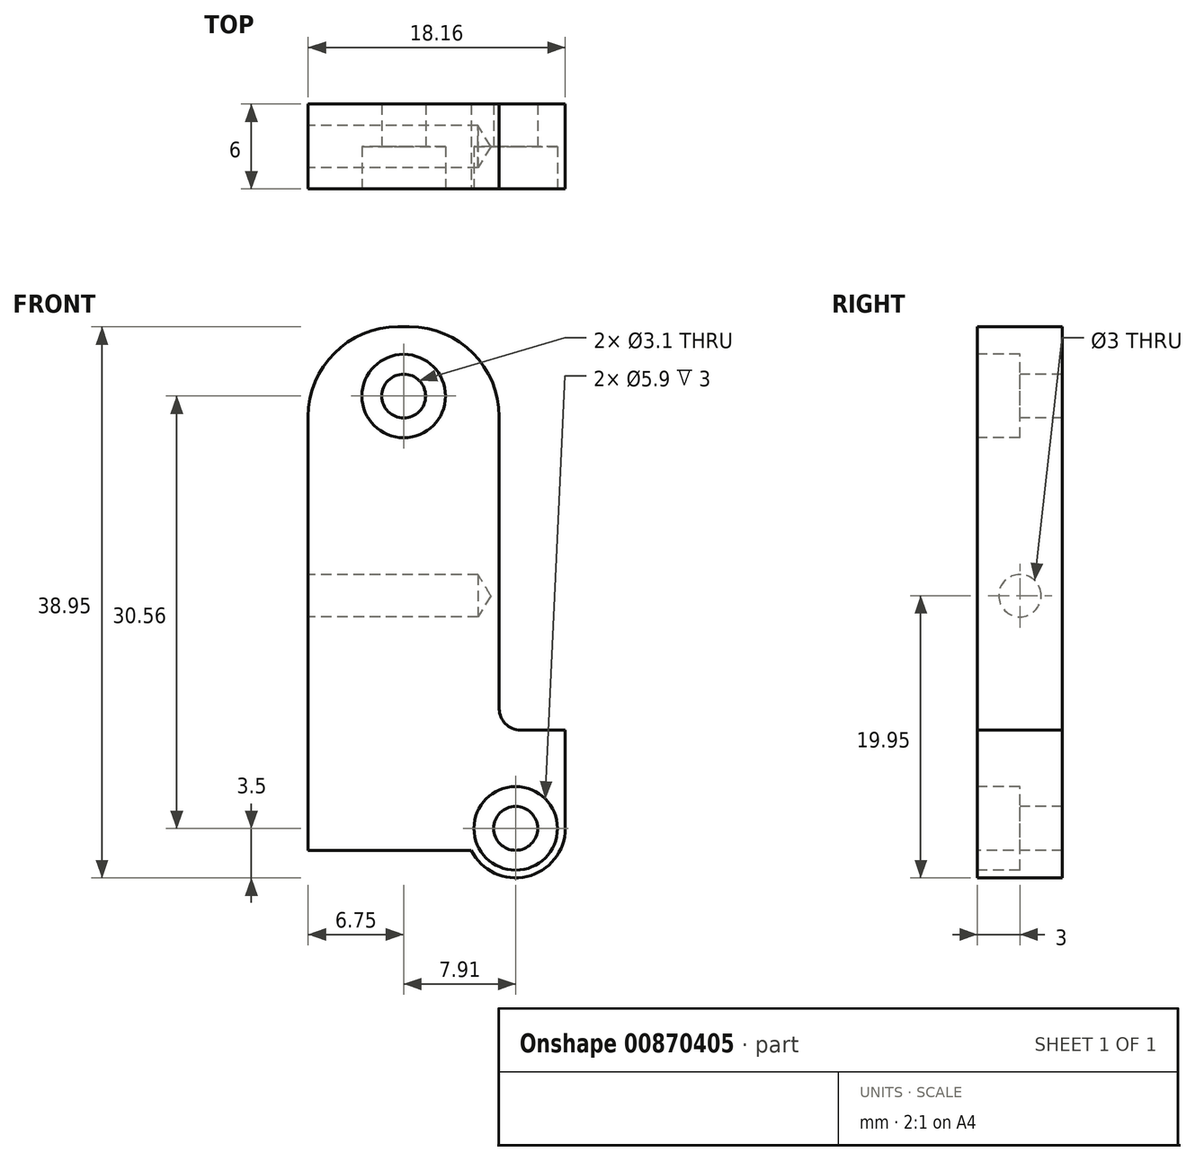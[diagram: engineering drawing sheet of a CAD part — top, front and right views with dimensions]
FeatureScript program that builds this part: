
annotation { "Feature Type Name" : "Feature", "Feature Type Description" : "" }
export const myFeature = defineFeature(function(context is Context, id is Id, definition is map)
    precondition{}
    {
        {
            var Q0;
            Q0=qCreatedBy(makeId("Front.planeOp"),FACE);
            var sketch = newSketch(context, id + "F0", { "sketchPlane" : qUnion([Q0])});
            skLineSegment(sketch, "E0", {"start": v(17.5, 0) * mm, "end": v(17.5, 0) * mm});
            skLineSegment(sketch, "E1", {"start": v(0, 37) * mm, "end": v(0, 37) * mm});
            skLineSegment(sketch, "E2", {"start": v(0, 30.65) * mm, "end": v(0, 0) * mm});
            skLineSegment(sketch, "E3", {"start": v(6.35, 37) * mm, "end": v(7.15, 37) * mm});
            skLineSegment(sketch, "E4", {"start": v(13.5, 30.65) * mm, "end": v(13.5, 10) * mm});
            skLineSegment(sketch, "E5", {"start": v(13.5, 8.5) * mm, "end": v(13.5, 8.5) * mm});
            skPoint(sketch, "E6.visualSharp", {"position": v(13.5, 8.5) * mm});
            skArc(sketch, "E6.filletArc", {"start": v(13.5, 10) * mm, "mid": v(13.94, 8.94) * mm, "end": v(15, 8.5) * mm});
            skArc(sketch, "E7.filletArc", {"start": v(6.35, 37) * mm, "mid": v(1.86, 35.14) * mm, "end": v(0, 30.65) * mm});
            skArc(sketch, "E8.filletArc", {"start": v(13.5, 30.65) * mm, "mid": v(11.64, 35.14) * mm, "end": v(7.15, 37) * mm});
            skLineSegment(sketch, "E9", {"start": v(6.75, 32.1) * mm, "end": v(6.75, -5.5) * mm, "construction": true});
            skLineSegment(sketch, "E10", {"start": v(-6.61, 1.55) * mm, "end": v(34.63, 1.55) * mm, "construction": true});
            skPoint(sketch, "E11", {"position": v(14.66, 1.55) * mm});
            skArc(sketch, "E12", {"start": v(11.52, 0) * mm, "mid": v(15.46, -1.86) * mm, "end": v(18.16, 1.55) * mm});
            skLineSegment(sketch, "E13", {"start": v(0, 0) * mm, "end": v(11.52, 0) * mm});
            skLineSegment(sketch, "E14", {"start": v(18.16, 1.55) * mm, "end": v(18.16, 8.5) * mm});
            skLineSegment(sketch, "E15", {"start": v(15, 8.5) * mm, "end": v(18.16, 8.5) * mm});
            skPoint(sketch, "E16", {"position": v(6.75, 32.1) * mm});
            skSolve(sketch);
        }
        {
            var Q0;
            Q0 = qSketchRegion(id + "F0", true);
            extrude(context, id + "F1", {"entities" : qUnion([Q0]), "oppositeDirection" : true, "depth" : 6 * mm, "offsetDistance" : 25 * mm});
        }
        {
            var Q0;
            Q0=sQuery(id+"F0.wireOp",VERTEX,"E9.start");
            var Q1;
            Q1=makeQuery(id+"F1.opExtrude","SWEPT_BODY",BODY,{"disambiguationData":[OSD([sQuery(id+"F0.wireOp",EDGE,"E2"),sQuery(id+"F0.wireOp",EDGE,"E3"),sQuery(id+"F0.wireOp",EDGE,"E4"),sQuery(id+"F0.wireOp",EDGE,"E6.filletArc"),sQuery(id+"F0.wireOp",EDGE,"E7.filletArc"),sQuery(id+"F0.wireOp",EDGE,"E8.filletArc"),sQuery(id+"F0.wireOp",EDGE,"E12"),sQuery(id+"F0.wireOp",EDGE,"E13"),sQuery(id+"F0.wireOp",EDGE,"E14"),sQuery(id+"F0.wireOp",EDGE,"E15")])]});
            hole(context, id + "F2", {"style" : HoleStyle.C_BORE, "endStyle" : HoleEndStyle.THROUGH, "holeDiameter" : 3.1 * mm, "cBoreDiameter" : 5.9 * mm, "cBoreDepth" : 3 * mm, "majorDiameter" : 5 * mm, "isTappedThrough" : true, "tappedDepth" : 12 * mm, "tapClearance" : 3, "locations" : qUnion([Q0]), "scope" : qUnion([Q1])});
        }
        {
            var Q0;
            Q0=sQuery(id+"F0.wireOp",VERTEX,"E11");
            var Q1;
            Q1=makeQuery(id+"F1.opExtrude","SWEPT_BODY",BODY,{"disambiguationData":[OSD([sQuery(id+"F0.wireOp",EDGE,"E2"),sQuery(id+"F0.wireOp",EDGE,"E3"),sQuery(id+"F0.wireOp",EDGE,"E4"),sQuery(id+"F0.wireOp",EDGE,"E6.filletArc"),sQuery(id+"F0.wireOp",EDGE,"E7.filletArc"),sQuery(id+"F0.wireOp",EDGE,"E8.filletArc"),sQuery(id+"F0.wireOp",EDGE,"E12"),sQuery(id+"F0.wireOp",EDGE,"E13"),sQuery(id+"F0.wireOp",EDGE,"E14"),sQuery(id+"F0.wireOp",EDGE,"E15")])]});
            hole(context, id + "F3", {"style" : HoleStyle.C_BORE, "endStyle" : HoleEndStyle.THROUGH, "holeDiameter" : 3.1 * mm, "cBoreDiameter" : 5.9 * mm, "cBoreDepth" : 3 * mm, "majorDiameter" : 5 * mm, "isTappedThrough" : true, "tappedDepth" : 12 * mm, "tapClearance" : 3, "locations" : qUnion([Q0]), "scope" : qUnion([Q1])});
        }
        {
            var Q0;
            Q0=makeQuery(id+"F1.opExtrude","SWEPT_FACE",FACE,{"disambiguationData":[OSD([sQuery(id+"F0.wireOp",EDGE,"E2")])]});
            var sketch = newSketch(context, id + "F4", { "sketchPlane" : qUnion([Q0])});
            skLineSegment(sketch, "E17", {"start": v(-6, 0) * mm, "end": v(0, 0) * mm, "construction": true});
            skLineSegment(sketch, "E18.0", {"start": v(-3, 30.65) * mm, "end": v(-3, 0) * mm, "construction": true});
            skPoint(sketch, "E19", {"position": v(-3, 18) * mm});
            skSolve(sketch);
        }
        {
            var Q0;
            Q0=sQuery(id+"F4.wireOp",VERTEX,"E19");
            var Q1;
            Q1=makeQuery(id+"F1.opExtrude","SWEPT_BODY",BODY,{"disambiguationData":[OSD([sQuery(id+"F0.wireOp",EDGE,"E2"),sQuery(id+"F0.wireOp",EDGE,"E3"),sQuery(id+"F0.wireOp",EDGE,"E4"),sQuery(id+"F0.wireOp",EDGE,"E6.filletArc"),sQuery(id+"F0.wireOp",EDGE,"E7.filletArc"),sQuery(id+"F0.wireOp",EDGE,"E8.filletArc"),sQuery(id+"F0.wireOp",EDGE,"E12"),sQuery(id+"F0.wireOp",EDGE,"E13"),sQuery(id+"F0.wireOp",EDGE,"E14"),sQuery(id+"F0.wireOp",EDGE,"E15")])]});
            hole(context, id + "F5", {"style" : HoleStyle.SIMPLE, "endStyle" : HoleEndStyle.BLIND, "holeDiameter" : 3 * mm, "majorDiameter" : 5 * mm, "holeDepth" : 12 * mm, "isTappedThrough" : true, "tappedDepth" : 12 * mm, "tapClearance" : 3, "locations" : qUnion([Q0]), "scope" : qUnion([Q1])});
        }
    });
